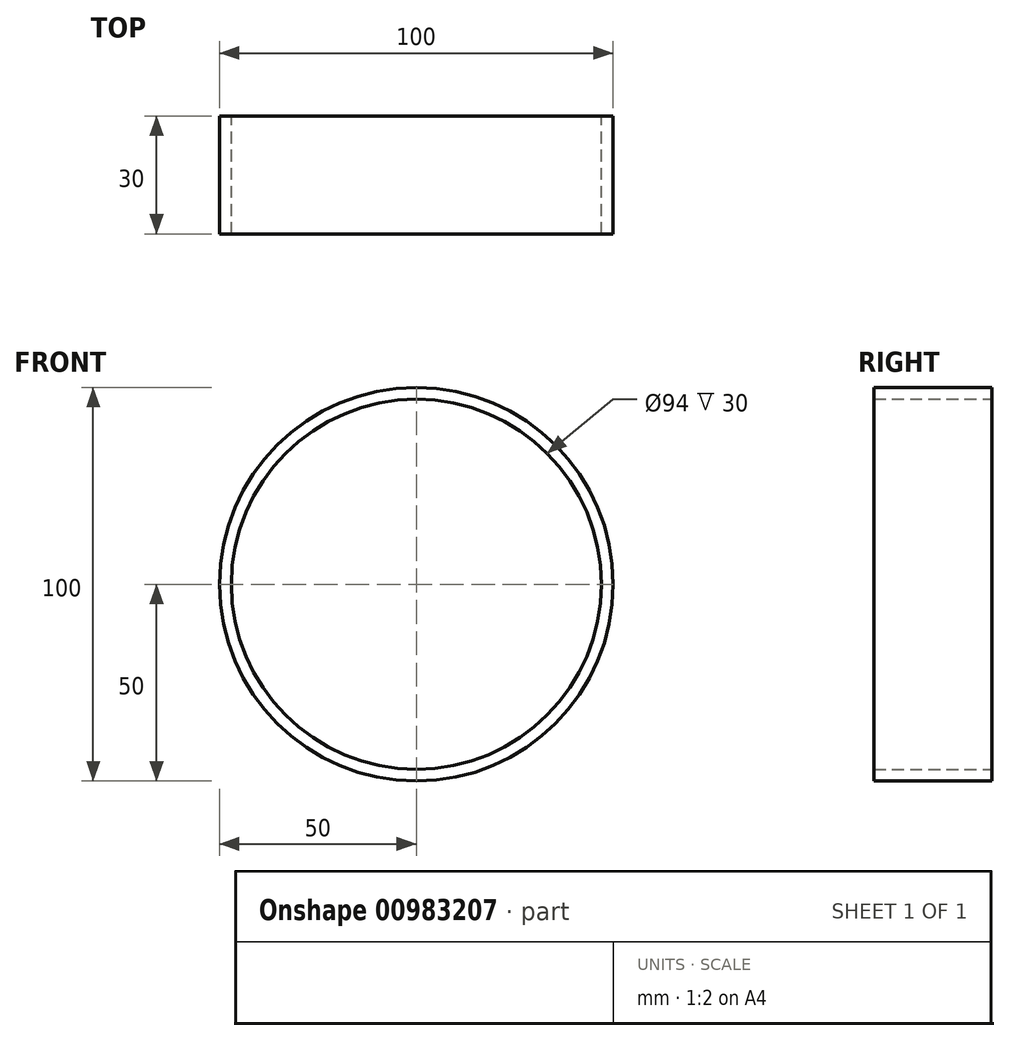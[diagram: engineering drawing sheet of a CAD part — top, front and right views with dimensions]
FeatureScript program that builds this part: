
annotation { "Feature Type Name" : "Feature", "Feature Type Description" : "" }
export const myFeature = defineFeature(function(context is Context, id is Id, definition is map)
    precondition{}
    {
        {
            var Q0;
            Q0=qCreatedBy(makeId("Front.planeOp"),FACE);
            var sketch = newSketch(context, id + "F0", { "sketchPlane" : qUnion([Q0])});
            skCircle(sketch, "E0", {"center": v(0, 0) * mm, "radius": 47 * mm});
            skCircle(sketch, "E1", {"center": v(0, 0) * mm, "radius": 50 * mm});
            skSolve(sketch);
        }
        {
            var Q0;
            Q0=makeQuery(id+"F0.imprint","IMPRINT",FACE,{"disambiguationData":[TD([[makeQuery(id+"F0.imprint","IMPRINT",EDGE,{"derivedFrom":sQuery(id+"F0.wireOp",EDGE,"E0")}),-1.0]])]});
            extrude(context, id + "F1", {"entities" : qUnion([Q0]), "depth" : 30 * mm, "offsetDistance" : 25 * mm});
        }
    });
